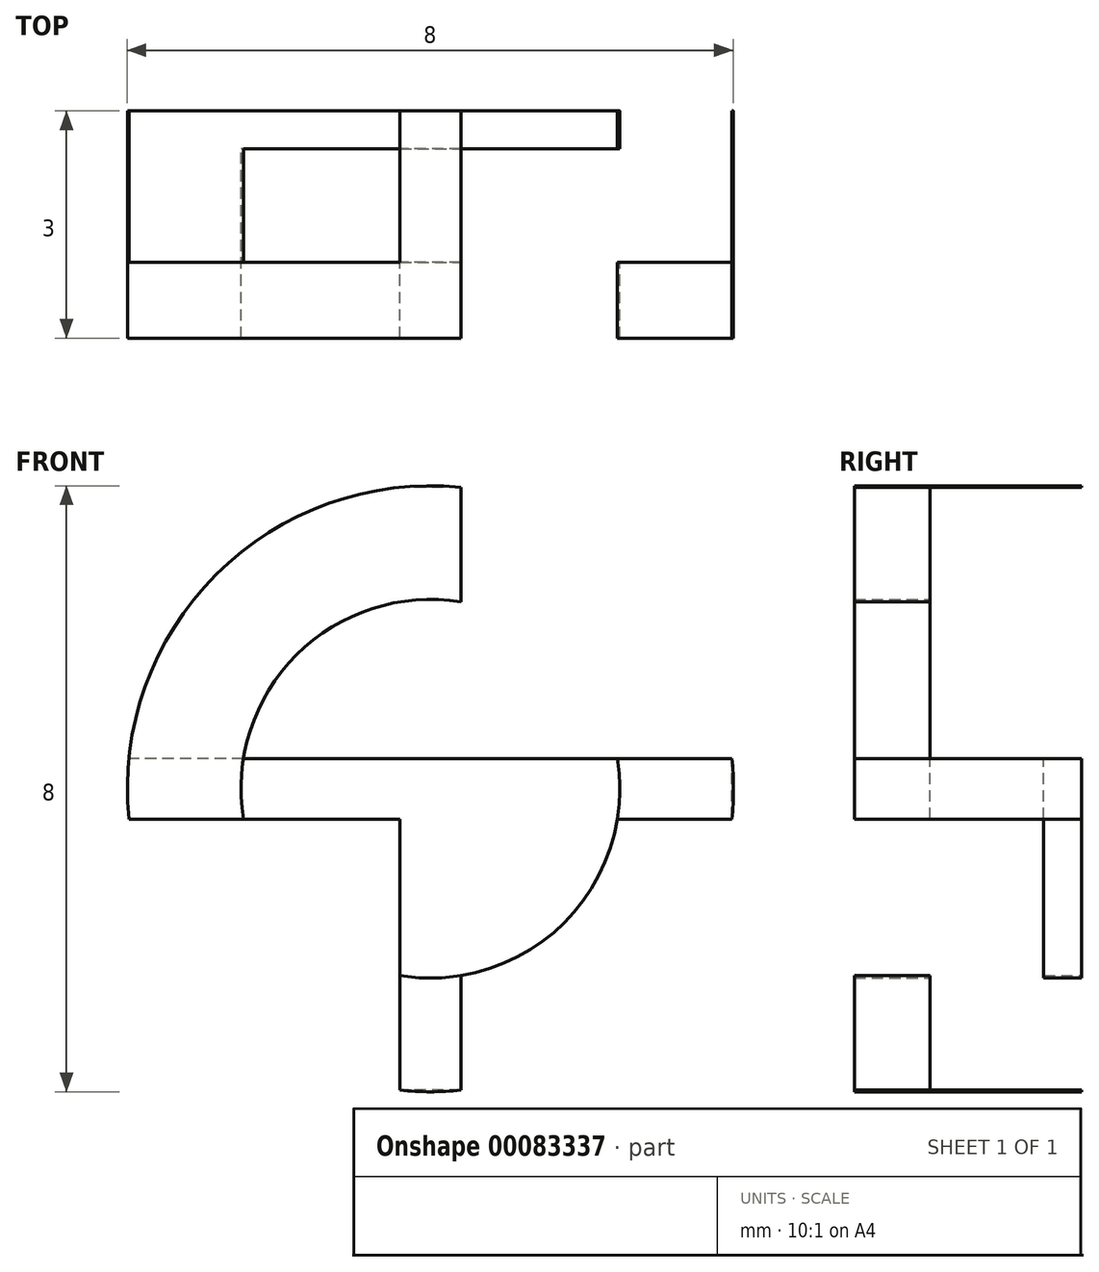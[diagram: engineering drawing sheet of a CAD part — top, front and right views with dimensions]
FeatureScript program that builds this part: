
annotation { "Feature Type Name" : "Feature", "Feature Type Description" : "" }
export const myFeature = defineFeature(function(context is Context, id is Id, definition is map)
    precondition{}
    {
        {
            var Q0;
            Q0=qCreatedBy(makeId("Front.planeOp"),FACE);
            var sketch = newSketch(context, id + "F0", { "sketchPlane" : qUnion([Q0])});
            skCircle(sketch, "E0", {"center": v(-6.32, -0.9) * mm, "radius": 2.5 * mm});
            skCircle(sketch, "E1", {"center": v(-6.32, -0.9) * mm, "radius": 4 * mm});
            skLineSegment(sketch, "E2.bottom", {"start": v(-2.34, -1.3) * mm, "end": v(-10.3, -1.3) * mm});
            skLineSegment(sketch, "E2.top", {"start": v(-2.34, -0.5) * mm, "end": v(-10.3, -0.5) * mm});
            skLineSegment(sketch, "E2.left", {"start": v(-2.34, -1.3) * mm, "end": v(-2.34, -0.5) * mm});
            skLineSegment(sketch, "E2.right", {"start": v(-10.3, -1.3) * mm, "end": v(-10.3, -0.5) * mm});
            skLineSegment(sketch, "E3.bottom", {"start": v(-5.92, 3.07) * mm, "end": v(-6.72, 3.07) * mm});
            skLineSegment(sketch, "E3.top", {"start": v(-5.92, -4.89) * mm, "end": v(-6.72, -4.89) * mm});
            skLineSegment(sketch, "E3.left", {"start": v(-5.92, 3.07) * mm, "end": v(-5.92, -4.89) * mm});
            skLineSegment(sketch, "E3.right", {"start": v(-6.72, 3.07) * mm, "end": v(-6.72, -4.89) * mm});
            skSolve(sketch);
        }
        {
            var Q0;
            {var subQ0=sQuery(id+"F0.wireOp",EDGE,"E2.bottom");var subQ1=sQuery(id+"F0.wireOp",EDGE,"E0");var subQ2=makeQuery(id+"F0.imprint","INTERSECT",VERTEX,{"disambiguationData":[OD(0.0)],"derivedFrom":[subQ1,subQ0]});Q0=makeQuery(id+"F0.imprint","IMPRINT",FACE,{"disambiguationData":[TD([[makeQuery(id+"F0.imprint","IMPRINT",EDGE,{"disambiguationData":[TD([[subQ2,-1.0]])],"derivedFrom":subQ1}),-1.0]])]});}
            var Q1;
            {var subQ5=sQuery(id+"F0.wireOp",EDGE,"E3.top");Q1=makeQuery(id+"F0.imprint","IMPRINT",FACE,{"disambiguationData":[TD([[makeQuery(id+"F0.imprint","IMPRINT",EDGE,{"derivedFrom":subQ5}),-1.0]])]});}
            var Q2;
            {var subQ0=sQuery(id+"F0.wireOp",EDGE,"E3.left");var subQ1=sQuery(id+"F0.wireOp",EDGE,"E0");var subQ2=makeQuery(id+"F0.imprint","INTERSECT",VERTEX,{"disambiguationData":[OD(1.0)],"derivedFrom":[subQ1,subQ0]});Q2=makeQuery(id+"F0.imprint","IMPRINT",FACE,{"disambiguationData":[TD([[makeQuery(id+"F0.imprint","IMPRINT",EDGE,{"disambiguationData":[TD([[subQ2,-1.0]])],"derivedFrom":subQ1}),-1.0]])]});}
            var Q3;
            {var subQ5=sQuery(id+"F0.wireOp",EDGE,"E2.left");Q3=makeQuery(id+"F0.imprint","IMPRINT",FACE,{"disambiguationData":[TD([[makeQuery(id+"F0.imprint","IMPRINT",EDGE,{"derivedFrom":subQ5}),1.0]])]});}
            var Q4;
            {var subQ0=sQuery(id+"F0.wireOp",EDGE,"E3.left");var subQ1=sQuery(id+"F0.wireOp",EDGE,"E0");var subQ2=makeQuery(id+"F0.imprint","INTERSECT",VERTEX,{"disambiguationData":[OD(0.0)],"derivedFrom":[subQ1,subQ0]});Q4=makeQuery(id+"F0.imprint","IMPRINT",FACE,{"disambiguationData":[TD([[makeQuery(id+"F0.imprint","IMPRINT",EDGE,{"disambiguationData":[TD([[subQ2,1.0]])],"derivedFrom":subQ1}),-1.0]])]});}
            var Q5;
            {var subQ5=sQuery(id+"F0.wireOp",EDGE,"E3.bottom");Q5=makeQuery(id+"F0.imprint","IMPRINT",FACE,{"disambiguationData":[TD([[makeQuery(id+"F0.imprint","IMPRINT",EDGE,{"derivedFrom":subQ5}),1.0]])]});}
            var Q6;
            {var subQ0=sQuery(id+"F0.wireOp",EDGE,"E3.right");var subQ1=sQuery(id+"F0.wireOp",EDGE,"E0");var subQ2=makeQuery(id+"F0.imprint","INTERSECT",VERTEX,{"disambiguationData":[OD(0.0)],"derivedFrom":[subQ1,subQ0]});Q6=makeQuery(id+"F0.imprint","IMPRINT",FACE,{"disambiguationData":[TD([[makeQuery(id+"F0.imprint","IMPRINT",EDGE,{"disambiguationData":[TD([[subQ2,-1.0]])],"derivedFrom":subQ1}),-1.0]])]});}
            var Q7;
            {var subQ5=sQuery(id+"F0.wireOp",EDGE,"E2.right");Q7=makeQuery(id+"F0.imprint","IMPRINT",FACE,{"disambiguationData":[TD([[makeQuery(id+"F0.imprint","IMPRINT",EDGE,{"derivedFrom":subQ5}),-1.0]])]});}
            var Q8;
            {var subQ0=sQuery(id+"F0.wireOp",EDGE,"E3.bottom");Q8=makeQuery(id+"F0.imprint","IMPRINT",FACE,{"disambiguationData":[TD([[makeQuery(id+"F0.imprint","IMPRINT",EDGE,{"derivedFrom":subQ0}),-1.0]])]});}
            var Q9;
            {var subQ0=sQuery(id+"F0.wireOp",EDGE,"E2.left");Q9=makeQuery(id+"F0.imprint","IMPRINT",FACE,{"disambiguationData":[TD([[makeQuery(id+"F0.imprint","IMPRINT",EDGE,{"derivedFrom":subQ0}),-1.0]])]});}
            var Q10;
            {var subQ0=sQuery(id+"F0.wireOp",EDGE,"E2.right");Q10=makeQuery(id+"F0.imprint","IMPRINT",FACE,{"disambiguationData":[TD([[makeQuery(id+"F0.imprint","IMPRINT",EDGE,{"derivedFrom":subQ0}),1.0]])]});}
            var Q11;
            {var subQ0=sQuery(id+"F0.wireOp",EDGE,"E3.top");Q11=makeQuery(id+"F0.imprint","IMPRINT",FACE,{"disambiguationData":[TD([[makeQuery(id+"F0.imprint","IMPRINT",EDGE,{"derivedFrom":subQ0}),1.0]])]});}
            extrude(context, id + "F1", {"entities" : qUnion([Q0, Q1, Q2, Q3, Q4, Q5, Q6, Q7, Q8, Q9, Q10, Q11]), "depth" : 3 * mm});
        }
        {
            var Q0;
            {var subQ0=sQuery(id+"F0.wireOp",EDGE,"E3.right");var subQ1=sQuery(id+"F0.wireOp",EDGE,"E0");var subQ2=makeQuery(id+"F0.imprint","INTERSECT",VERTEX,{"disambiguationData":[OD(1.0)],"derivedFrom":[subQ1,subQ0]});Q0=makeQuery(id+"F0.imprint","IMPRINT",FACE,{"disambiguationData":[TD([[makeQuery(id+"F0.imprint","IMPRINT",EDGE,{"disambiguationData":[TD([[subQ2,-1.0]])],"derivedFrom":subQ1}),1.0]])]});}
            var Q1;
            {var subQ0=sQuery(id+"F0.wireOp",EDGE,"E3.left");var subQ1=sQuery(id+"F0.wireOp",EDGE,"E2.bottom");var subQ2=makeQuery(id+"F0.imprint","INTERSECT",VERTEX,{"derivedFrom":[subQ1,subQ0]});Q1=makeQuery(id+"F0.imprint","IMPRINT",FACE,{"disambiguationData":[TD([[makeQuery(id+"F0.imprint","IMPRINT",EDGE,{"disambiguationData":[TD([[subQ2,-1.0]])],"derivedFrom":subQ1}),-1.0]])]});}
            var Q2;
            {var subQ0=sQuery(id+"F0.wireOp",EDGE,"E2.top");var subQ1=sQuery(id+"F0.wireOp",EDGE,"E0");var subQ2=makeQuery(id+"F0.imprint","INTERSECT",VERTEX,{"disambiguationData":[OD(1.0)],"derivedFrom":[subQ1,subQ0]});Q2=makeQuery(id+"F0.imprint","IMPRINT",FACE,{"disambiguationData":[TD([[makeQuery(id+"F0.imprint","IMPRINT",EDGE,{"disambiguationData":[TD([[subQ2,-1.0]])],"derivedFrom":subQ1}),1.0]])]});}
            var Q3;
            {var subQ0=sQuery(id+"F0.wireOp",EDGE,"E3.left");var subQ1=sQuery(id+"F0.wireOp",EDGE,"E0");var subQ2=makeQuery(id+"F0.imprint","INTERSECT",VERTEX,{"disambiguationData":[OD(0.0)],"derivedFrom":[subQ1,subQ0]});Q3=makeQuery(id+"F0.imprint","IMPRINT",FACE,{"disambiguationData":[TD([[makeQuery(id+"F0.imprint","IMPRINT",EDGE,{"disambiguationData":[TD([[subQ2,-1.0]])],"derivedFrom":subQ1}),1.0]])]});}
            var Q4;
            {var subQ0=sQuery(id+"F0.wireOp",EDGE,"E2.top");var subQ1=sQuery(id+"F0.wireOp",EDGE,"E0");var subQ2=makeQuery(id+"F0.imprint","INTERSECT",VERTEX,{"disambiguationData":[OD(0.0)],"derivedFrom":[subQ1,subQ0]});Q4=makeQuery(id+"F0.imprint","IMPRINT",FACE,{"disambiguationData":[TD([[makeQuery(id+"F0.imprint","IMPRINT",EDGE,{"disambiguationData":[TD([[subQ2,1.0]])],"derivedFrom":subQ1}),1.0]])]});}
            extrude(context, id + "F2", {"entities" : qUnion([Q0, Q1, Q2, Q3, Q4]), "operationType" : NewBodyOperationType.ADD, "depth" : 0.5 * mm});
        }
        {
            var Q0;
            {var subQ0=sQuery(id+"F0.wireOp",EDGE,"E3.left");var subQ1=sQuery(id+"F0.wireOp",EDGE,"E0");var subQ2=makeQuery(id+"F0.imprint","INTERSECT",VERTEX,{"disambiguationData":[OD(1.0)],"derivedFrom":[subQ1,subQ0]});Q0=makeQuery(id+"F0.imprint","IMPRINT",FACE,{"disambiguationData":[TD([[makeQuery(id+"F0.imprint","IMPRINT",EDGE,{"disambiguationData":[TD([[subQ2,-1.0]])],"derivedFrom":subQ1}),-1.0]])]});}
            var Q1;
            {var subQ0=sQuery(id+"F0.wireOp",EDGE,"E2.bottom");var subQ1=sQuery(id+"F0.wireOp",EDGE,"E0");var subQ2=makeQuery(id+"F0.imprint","INTERSECT",VERTEX,{"disambiguationData":[OD(0.0)],"derivedFrom":[subQ1,subQ0]});Q1=makeQuery(id+"F0.imprint","IMPRINT",FACE,{"disambiguationData":[TD([[makeQuery(id+"F0.imprint","IMPRINT",EDGE,{"disambiguationData":[TD([[subQ2,-1.0]])],"derivedFrom":subQ1}),-1.0]])]});}
            var Q2;
            {var subQ0=sQuery(id+"F0.wireOp",EDGE,"E3.right");var subQ1=sQuery(id+"F0.wireOp",EDGE,"E0");var subQ2=makeQuery(id+"F0.imprint","INTERSECT",VERTEX,{"disambiguationData":[OD(0.0)],"derivedFrom":[subQ1,subQ0]});Q2=makeQuery(id+"F0.imprint","IMPRINT",FACE,{"disambiguationData":[TD([[makeQuery(id+"F0.imprint","IMPRINT",EDGE,{"disambiguationData":[TD([[subQ2,-1.0]])],"derivedFrom":subQ1}),-1.0]])]});}
            var Q3;
            {var subQ0=sQuery(id+"F0.wireOp",EDGE,"E3.left");var subQ1=sQuery(id+"F0.wireOp",EDGE,"E0");var subQ2=makeQuery(id+"F0.imprint","INTERSECT",VERTEX,{"disambiguationData":[OD(0.0)],"derivedFrom":[subQ1,subQ0]});Q3=makeQuery(id+"F0.imprint","IMPRINT",FACE,{"disambiguationData":[TD([[makeQuery(id+"F0.imprint","IMPRINT",EDGE,{"disambiguationData":[TD([[subQ2,1.0]])],"derivedFrom":subQ1}),-1.0]])]});}
            extrude(context, id + "F3", {"entities" : qUnion([Q0, Q1, Q2, Q3]), "operationType" : NewBodyOperationType.REMOVE, "depth" : 2 * mm});
        }
    });
